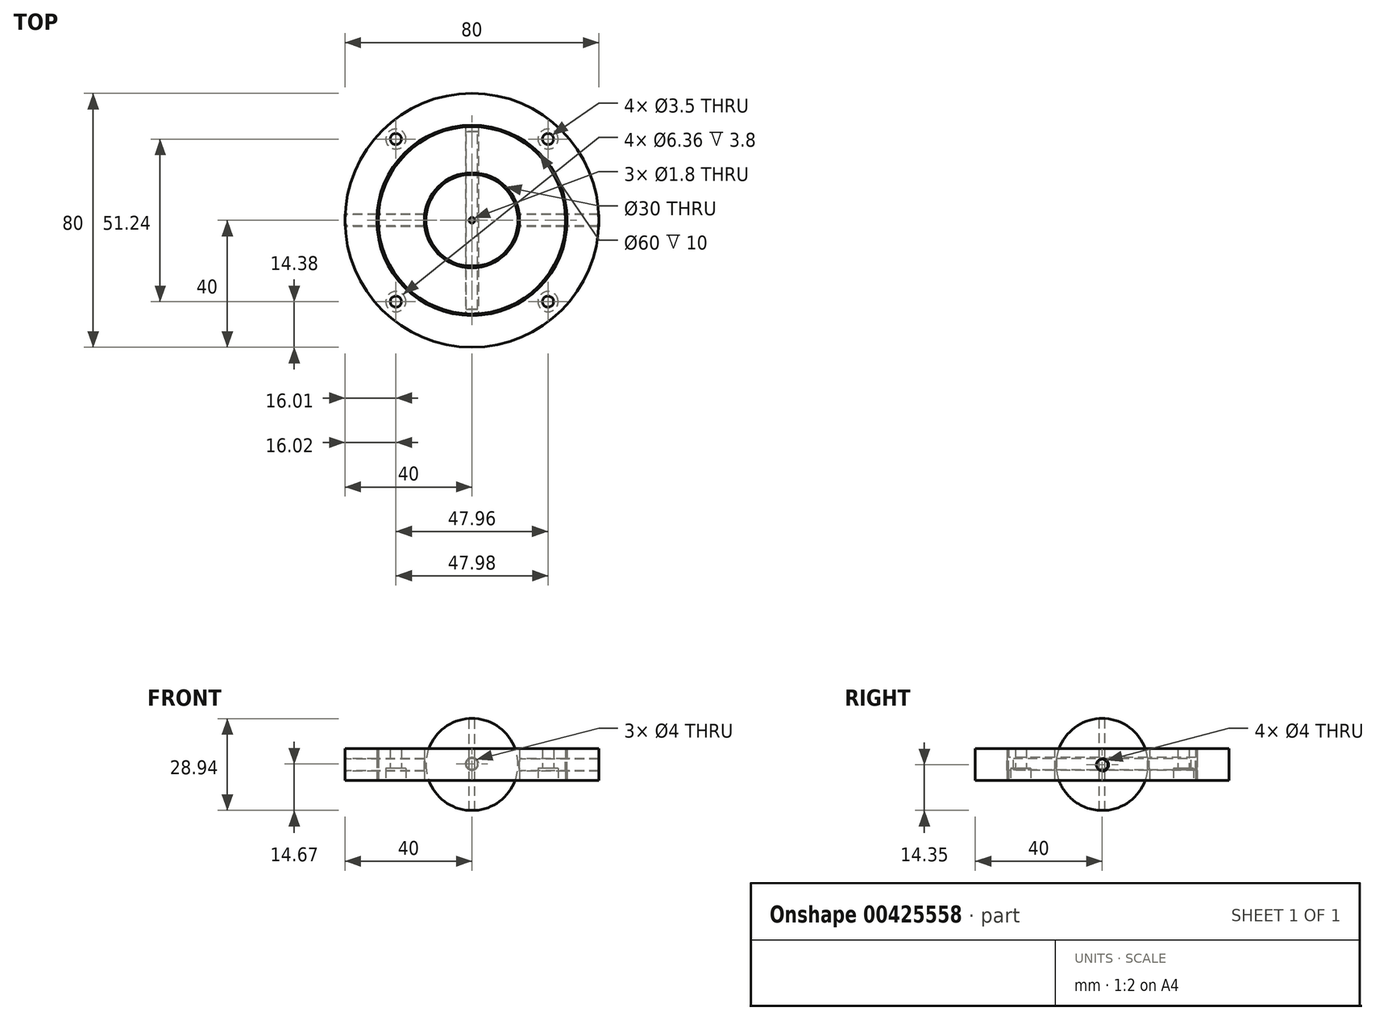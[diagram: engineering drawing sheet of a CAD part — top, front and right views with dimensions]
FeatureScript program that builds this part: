
annotation { "Feature Type Name" : "Feature", "Feature Type Description" : "" }
export const myFeature = defineFeature(function(context is Context, id is Id, definition is map)
    precondition{}
    {
        {
            var Q0;
            Q0=qCreatedBy(makeId("Top.planeOp"),FACE);
            var sketch = newSketch(context, id + "F0", { "sketchPlane" : qUnion([Q0])});
            skCircle(sketch, "E0", {"center": v(0, 0) * mm, "radius": 20 * mm});
            skCircle(sketch, "E1", {"center": v(0, 0) * mm, "radius": 15 * mm});
            skSolve(sketch);
        }
        {
            var Q0;
            Q0=makeQuery(id+"F0.imprint","IMPRINT",FACE,{"disambiguationData":[TD([[makeQuery(id+"F0.imprint","IMPRINT",EDGE,{"derivedFrom":sQuery(id+"F0.wireOp",EDGE,"E0")}),1.0]])]});
            extrude(context, id + "F1", {"entities" : qUnion([Q0]), "depth" : 5 * mm});
        }
        {
            var Q0;
            Q0=qCreatedBy(makeId("Right.planeOp"),FACE);
            var sketch = newSketch(context, id + "F2", { "sketchPlane" : qUnion([Q0])});
            skCircle(sketch, "E2", {"center": v(0, 2.44) * mm, "radius": 1 * mm});
            skSolve(sketch);
        }
        {
            var Q0;
            Q0 = qSketchRegion(id + "F2", true);
            extrude(context, id + "F3", {"entities" : qUnion([Q0]), "operationType" : NewBodyOperationType.REMOVE, "depth" : 25 * mm, "hasSecondDirection" : true, "secondDirectionOppositeDirection" : true, "secondDirectionDepth" : 25 * mm});
        }
        {
            var Q0;
            Q0=qCreatedBy(makeId("Top.planeOp"),FACE);
            var sketch = newSketch(context, id + "F4", { "sketchPlane" : qUnion([Q0])});
            skCircle(sketch, "E3", {"center": v(0, 0) * mm, "radius": 14.75 * mm});
            skCircle(sketch, "E4", {"center": v(0, 0) * mm, "radius": 7.5 * mm});
            skSolve(sketch);
        }
        {
            var Q0;
            Q0=makeQuery(id+"F4.imprint","IMPRINT",FACE,{"disambiguationData":[TD([[makeQuery(id+"F4.imprint","IMPRINT",EDGE,{"derivedFrom":sQuery(id+"F4.wireOp",EDGE,"E3")}),1.0]])]});
            extrude(context, id + "F5", {"entities" : qUnion([Q0]), "depth" : 5 * mm});
        }
        {
            var Q0;
            Q0=qCreatedBy(makeId("Right.planeOp"),FACE);
            var sketch = newSketch(context, id + "F6", { "sketchPlane" : qUnion([Q0])});
            skCircle(sketch, "E5", {"center": v(0, 2.43) * mm, "radius": 0.9 * mm});
            skSolve(sketch);
        }
        {
            var Q0;
            Q0 = qSketchRegion(id + "F6", true);
            extrude(context, id + "F7", {"entities" : qUnion([Q0]), "endBound" : BoundingType.SYMMETRIC, "depth" : 40 * mm});
        }
        {
            var Q0;
            Q0=makeQuery(id+"F4.imprint","IMPRINT",FACE,{"disambiguationData":[TD([[makeQuery(id+"F4.imprint","IMPRINT",EDGE,{"derivedFrom":sQuery(id+"F4.wireOp",EDGE,"E4")}),1.0]])]});
            extrude(context, id + "F8", {"entities" : qUnion([Q0]), "operationType" : NewBodyOperationType.REMOVE, "endBound" : BoundingType.SYMMETRIC, "oppositeDirection" : true, "depth" : 25 * mm});
        }
        {
            var Q0;
            Q0=qCreatedBy(makeId("Top.planeOp"),FACE);
            var sketch = newSketch(context, id + "F9", { "sketchPlane" : qUnion([Q0])});
            skCircle(sketch, "E6", {"center": v(0, 0) * mm, "radius": 7.25 * mm});
            skLineSegment(sketch, "E7", {"start": v(-7.25, 0) * mm, "end": v(7.25, 0) * mm});
            skSolve(sketch);
        }
        {
            var Q0;
            {var subQ0=sQuery(id+"F9.wireOp",EDGE,"E7");Q0=makeQuery(id+"F9.imprint","IMPRINT",FACE,{"disambiguationData":[TD([[makeQuery(id+"F9.imprint","IMPRINT",EDGE,{"derivedFrom":subQ0}),1.0]])]});}
            var Q1;
            Q1=sQuery(id+"F9.wireOp",EDGE,"E7");
            revolve(context, id + "F10", {"entities" : qUnion([Q0]), "axis" : qUnion([Q1]), "revolveType" : RevolveType.FULL});
        }
        {
            var Q0;
            Q0=makeQuery(id+"F10.opRevolve","SWEPT_BODY",BODY,{"disambiguationData":[OSD([sQuery(id+"F9.wireOp",EDGE,"E6"),sQuery(id+"F9.wireOp",EDGE,"E7")])]});
            var Q1;
            Q1=qCreatedBy(makeId("Top.planeOp"),FACE);
            transform(context, id + "F11", {"entities" : qUnion([Q0]), "transformType" : TransformType.TRANSLATION_DISTANCE, "transformDirection" : qUnion([Q1]), "distance" : 2.5 * mm, "makeCopy" : false});
        }
        {
            var Q0;
            Q0=makeQuery(id+"F10.opRevolve","SWEPT_BODY",BODY,{"disambiguationData":[OSD([sQuery(id+"F9.wireOp",EDGE,"E6"),sQuery(id+"F9.wireOp",EDGE,"E7")])]});
            transform(context, id + "F12", {"entities" : qUnion([Q0]), "transformType" : TransformType.TRANSLATION_3D, "dx" : 0 * mm, "dy" : 0 * mm, "dz" : 100 * mm, "makeCopy" : false});
        }
        {
            var Q0;
            Q0=qCreatedBy(makeId("Front.planeOp"),FACE);
            var sketch = newSketch(context, id + "F13", { "sketchPlane" : qUnion([Q0])});
            skCircle(sketch, "E8", {"center": v(0, 2.6) * mm, "radius": 1 * mm});
            skSolve(sketch);
        }
        {
            var Q0;
            Q0 = qSketchRegion(id + "F13", true);
            extrude(context, id + "F14", {"entities" : qUnion([Q0]), "operationType" : NewBodyOperationType.REMOVE, "endBound" : BoundingType.SYMMETRIC, "oppositeDirection" : true, "depth" : 30 * mm});
        }
        {
            var Q0;
            Q0=makeQuery(id+"F10.opRevolve","SWEPT_BODY",BODY,{"disambiguationData":[OSD([sQuery(id+"F9.wireOp",EDGE,"E6"),sQuery(id+"F9.wireOp",EDGE,"E7")])]});
            transform(context, id + "F15", {"entities" : qUnion([Q0]), "transformType" : TransformType.TRANSLATION_3D, "dx" : 0 * mm, "dy" : 0 * mm, "dz" : -100 * mm, "makeCopy" : false});
        }
        {
            var Q0;
            Q0=qCreatedBy(makeId("Front.planeOp"),FACE);
            var sketch = newSketch(context, id + "F16", { "sketchPlane" : qUnion([Q0])});
            skCircle(sketch, "E9", {"center": v(0, 2.6) * mm, "radius": 0.9 * mm});
            skSolve(sketch);
        }
        {
            var Q0;
            Q0=makeQuery(id+"F1.opExtrude","SWEPT_BODY",BODY,{"disambiguationData":[OSD([sQuery(id+"F0.wireOp",EDGE,"E0"),sQuery(id+"F0.wireOp",EDGE,"E1")])]});
            transform(context, id + "F17", {"entities" : qUnion([Q0]), "transformType" : TransformType.TRANSLATION_3D, "dx" : 0 * mm, "dy" : 0 * mm, "dz" : 100 * mm, "makeCopy" : false});
        }
        {
            var Q0;
            Q0=makeQuery(id+"F10.opRevolve","SWEPT_BODY",BODY,{"disambiguationData":[OSD([sQuery(id+"F9.wireOp",EDGE,"E6"),sQuery(id+"F9.wireOp",EDGE,"E7")])]});
            transform(context, id + "F18", {"entities" : qUnion([Q0]), "transformType" : TransformType.TRANSLATION_3D, "dx" : 0 * mm, "dy" : 0 * mm, "dz" : 50 * mm, "makeCopy" : false});
        }
        {
            var Q0;
            Q0=makeQuery(id+"F7.opExtrude","SWEPT_BODY",BODY,{"disambiguationData":[OSD([sQuery(id+"F6.wireOp",EDGE,"E5")])]});
            transform(context, id + "F19", {"entities" : qUnion([Q0]), "transformType" : TransformType.TRANSLATION_3D, "dx" : 50 * mm, "dy" : 0 * mm, "dz" : 0 * mm, "makeCopy" : false});
        }
        {
            var Q0;
            Q0 = qSketchRegion(id + "F2", true);
            extrude(context, id + "F20", {"entities" : qUnion([Q0]), "operationType" : NewBodyOperationType.REMOVE, "endBound" : BoundingType.SYMMETRIC, "depth" : 30 * mm});
        }
        {
            var Q0;
            Q0=makeQuery(id+"F10.opRevolve","SWEPT_BODY",BODY,{"disambiguationData":[OSD([sQuery(id+"F9.wireOp",EDGE,"E6"),sQuery(id+"F9.wireOp",EDGE,"E7")])]});
            transform(context, id + "F21", {"entities" : qUnion([Q0]), "transformType" : TransformType.TRANSLATION_3D, "dx" : 0 * mm, "dy" : 0 * mm, "dz" : -50 * mm, "makeCopy" : false});
        }
        {
            var Q0;
            Q0=qCreatedBy(makeId("Front.planeOp"),FACE);
            var sketch = newSketch(context, id + "F22", { "sketchPlane" : qUnion([Q0])});
            skCircle(sketch, "E10", {"center": v(0, 2.6) * mm, "radius": 1 * mm});
            skSolve(sketch);
        }
        {
            var Q0;
            Q0 = qSketchRegion(id + "F22", true);
            extrude(context, id + "F23", {"entities" : qUnion([Q0]), "operationType" : NewBodyOperationType.REMOVE, "endBound" : BoundingType.SYMMETRIC, "oppositeDirection" : true, "depth" : 15 * mm});
        }
        {
            var Q0;
            Q0=makeQuery(id+"F10.opRevolve","SWEPT_BODY",BODY,{"disambiguationData":[OSD([sQuery(id+"F9.wireOp",EDGE,"E6"),sQuery(id+"F9.wireOp",EDGE,"E7")])]});
            transform(context, id + "F24", {"entities" : qUnion([Q0]), "transformType" : TransformType.TRANSLATION_3D, "dx" : 0 * mm, "dy" : 0 * mm, "dz" : 50 * mm, "makeCopy" : false});
        }
        {
            var Q0;
            Q0=makeQuery(id+"F10.opRevolve","SWEPT_BODY",BODY,{"disambiguationData":[OSD([sQuery(id+"F9.wireOp",EDGE,"E6"),sQuery(id+"F9.wireOp",EDGE,"E7")])]});
            transform(context, id + "F25", {"entities" : qUnion([Q0]), "transformType" : TransformType.TRANSLATION_3D, "dx" : 0 * mm, "dy" : 0 * mm, "dz" : -50 * mm, "makeCopy" : false});
        }
        {
            var Q0;
            Q0 = qSketchRegion(id + "F16", true);
            extrude(context, id + "F26", {"entities" : qUnion([Q0]), "endBound" : BoundingType.SYMMETRIC, "depth" : 28 * mm});
        }
        {
            var Q0;
            Q0=makeQuery(id+"F1.opExtrude","SWEPT_BODY",BODY,{"disambiguationData":[OSD([sQuery(id+"F0.wireOp",EDGE,"E0"),sQuery(id+"F0.wireOp",EDGE,"E1")])]});
            var Q1;
            Q1=makeQuery(id+"F10.opRevolve","SWEPT_BODY",BODY,{"disambiguationData":[OSD([sQuery(id+"F9.wireOp",EDGE,"E6"),sQuery(id+"F9.wireOp",EDGE,"E7")])]});
            var Q2;
            Q2=makeQuery(id+"F7.opExtrude","SWEPT_BODY",BODY,{"disambiguationData":[OSD([sQuery(id+"F6.wireOp",EDGE,"E5")])]});
            var Q3;
            Q3=makeQuery(id+"F5.opExtrude","SWEPT_BODY",BODY,{"disambiguationData":[OSD([sQuery(id+"F4.wireOp",EDGE,"E3"),sQuery(id+"F4.wireOp",EDGE,"E4")])]});
            var Q4;
            Q4=makeQuery(id+"F26.opExtrude","SWEPT_BODY",BODY,{"disambiguationData":[OSD([sQuery(id+"F16.wireOp",EDGE,"E9")])]});
            var Q5;
            Q5=qCreatedBy(makeId("Origin.pointOp"),VERTEX);
            transform(context, id + "F27", {"entities" : qUnion([Q0, Q1, Q2, Q3, Q4]), "transformType" : TransformType.SCALE_UNIFORMLY, "scale" : 2, "scalePoint" : qUnion([Q5]), "makeCopy" : false});
        }
        {
            var Q0;
            Q0=qCreatedBy(makeId("Top.planeOp"),FACE);
            var sketch = newSketch(context, id + "F28", { "sketchPlane" : qUnion([Q0])});
            skCircle(sketch, "E11", {"center": v(0, 0) * mm, "radius": 0.9 * mm});
            skSolve(sketch);
        }
        {
            var Q0;
            Q0 = qSketchRegion(id + "F28", true);
            extrude(context, id + "F29", {"entities" : qUnion([Q0]), "operationType" : NewBodyOperationType.REMOVE, "endBound" : BoundingType.SYMMETRIC, "oppositeDirection" : true, "depth" : 40 * mm});
        }
        {
            var Q0;
            Q0=makeQuery(id+"F1.opExtrude","SWEPT_BODY",BODY,{"disambiguationData":[OSD([sQuery(id+"F0.wireOp",EDGE,"E0"),sQuery(id+"F0.wireOp",EDGE,"E1")])]});
            transform(context, id + "F30", {"entities" : qUnion([Q0]), "transformType" : TransformType.TRANSLATION_3D, "dx" : 0 * mm, "dy" : 0 * mm, "dz" : -200 * mm, "makeCopy" : false});
        }
        {
            var Q0;
            Q0=makeQuery(id+"F7.opExtrude","SWEPT_BODY",BODY,{"disambiguationData":[OSD([sQuery(id+"F6.wireOp",EDGE,"E5")])]});
            transform(context, id + "F31", {"entities" : qUnion([Q0]), "transformType" : TransformType.TRANSLATION_3D, "dx" : -100 * mm, "dy" : 0 * mm, "dz" : 0 * mm, "makeCopy" : false});
        }
        {
            var Q0;
            Q0=qCreatedBy(makeId("Top.planeOp"),FACE);
            var sketch = newSketch(context, id + "F32", { "sketchPlane" : qUnion([Q0])});
            skCircle(sketch, "E12", {"center": v(-23.99, 25.62) * mm, "radius": 1.75 * mm});
            skCircle(sketch, "E13.MirrorC", {"center": v(-23.99, -25.62) * mm, "radius": 1.75 * mm});
            skCircle(sketch, "E14.MirrorC", {"center": v(23.99, -25.62) * mm, "radius": 1.75 * mm});
            skCircle(sketch, "E15.MirrorC", {"center": v(23.99, 25.62) * mm, "radius": 1.75 * mm});
            skSolve(sketch);
        }
        {
            var Q0;
            Q0 = qSketchRegion(id + "F32", true);
            extrude(context, id + "F33", {"entities" : qUnion([Q0]), "operationType" : NewBodyOperationType.REMOVE, "oppositeDirection" : true, "depth" : -25.4 * mm});
        }
        {
            var Q0;
            Q0=qCreatedBy(makeId("Top.planeOp"),FACE);
            var sketch = newSketch(context, id + "F34", { "sketchPlane" : qUnion([Q0])});
            skLineSegment(sketch, "E16", {"start": v(-23.98, 23.86) * mm, "end": v(-23.98, 27.38) * mm});
            skLineSegment(sketch, "E17", {"start": v(-22.23, 25.62) * mm, "end": v(-25.75, 25.62) * mm});
            skCircle(sketch, "E18", {"center": v(-23.98, 25.62) * mm, "radius": 3.18 * mm});
            skPoint(sketch, "E18.centerSnap0", {"position": v(-23.99, 25.62) * mm});
            skCircle(sketch, "E19.MirrorC", {"center": v(-23.98, -25.62) * mm, "radius": 3.18 * mm});
            skCircle(sketch, "E20.MirrorC", {"center": v(23.98, -25.62) * mm, "radius": 3.18 * mm});
            skCircle(sketch, "E21.MirrorC", {"center": v(23.98, 25.62) * mm, "radius": 3.18 * mm});
            skSolve(sketch);
        }
        {
            var Q0;
            Q0=makeQuery(id+"F34.imprint","IMPRINT",FACE,{"disambiguationData":[TD([[makeQuery(id+"F34.imprint","IMPRINT",EDGE,{"derivedFrom":sQuery(id+"F34.wireOp",EDGE,"E18")}),1.0]])]});
            extrude(context, id + "F35", {"entities" : qUnion([Q0]), "operationType" : NewBodyOperationType.REMOVE, "oppositeDirection" : true, "depth" : -3.8 * mm});
        }
        {
            var Q0;
            Q0 = qSketchRegion(id + "F34", true);
            extrude(context, id + "F36", {"entities" : qUnion([Q0]), "operationType" : NewBodyOperationType.REMOVE, "oppositeDirection" : true, "depth" : -3.8 * mm});
        }
    });
